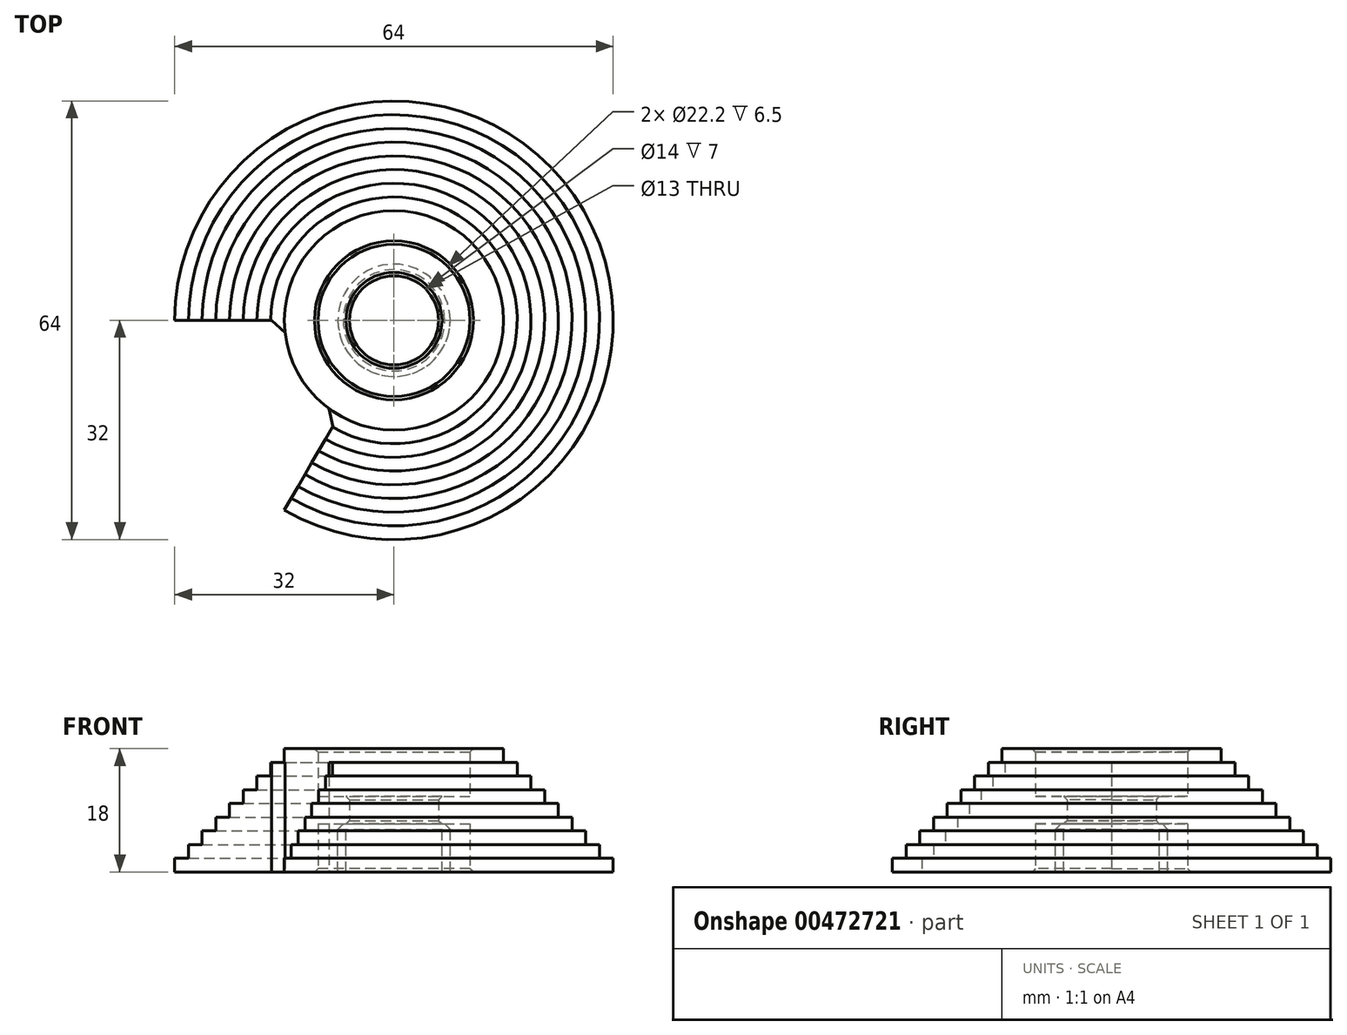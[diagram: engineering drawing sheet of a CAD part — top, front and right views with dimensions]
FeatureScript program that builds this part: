
annotation { "Feature Type Name" : "Feature", "Feature Type Description" : "" }
export const myFeature = defineFeature(function(context is Context, id is Id, definition is map)
    precondition{}
    {
        {
            var Q0;
            Q0=qCreatedBy(makeId("Front.planeOp"),FACE);
            var sketch = newSketch(context, id + "F0", { "sketchPlane" : qUnion([Q0])});
            skLineSegment(sketch, "E0", {"start": v(-11.1, 2) * mm, "end": v(-11.1, 9) * mm});
            skLineSegment(sketch, "E1", {"start": v(-11.1, 9) * mm, "end": v(-14, 9) * mm});
            skLineSegment(sketch, "E2", {"start": v(-14, 9) * mm, "end": v(-32, -9) * mm, "construction": true});
            skLineSegment(sketch, "E3", {"start": v(-32, -9) * mm, "end": v(-11.1, -9) * mm});
            skLineSegment(sketch, "E4", {"start": v(-11.1, -9) * mm, "end": v(-11.1, -2) * mm});
            skLineSegment(sketch, "E5", {"start": v(-11.1, 2) * mm, "end": v(-6.5, 2) * mm});
            skLineSegment(sketch, "E6", {"start": v(-6.5, 2) * mm, "end": v(-6.5, -2) * mm});
            skLineSegment(sketch, "E7", {"start": v(-6.5, -2) * mm, "end": v(-11.1, -2) * mm});
            skLineSegment(sketch, "E8", {"start": v(0, -9) * mm, "end": v(0, 9) * mm, "construction": true});
            skLineSegment(sketch, "E9", {"start": v(0, -9) * mm, "end": v(-32, -9) * mm, "construction": true});
            skLineSegment(sketch, "E10", {"start": v(-32, -9) * mm, "end": v(-32, -7) * mm});
            skLineSegment(sketch, "E11", {"start": v(-32, -7) * mm, "end": v(-30, -7) * mm});
            skLineSegment(sketch, "E12", {"start": v(-30, -7) * mm, "end": v(-30, -5) * mm});
            skLineSegment(sketch, "E13", {"start": v(-30, -5) * mm, "end": v(-28, -5) * mm});
            skLineSegment(sketch, "E14", {"start": v(-28, -5) * mm, "end": v(-28, -3) * mm});
            skLineSegment(sketch, "E15", {"start": v(-28, -3) * mm, "end": v(-26, -3) * mm});
            skLineSegment(sketch, "E16", {"start": v(-26, -3) * mm, "end": v(-26, -1) * mm});
            skLineSegment(sketch, "E17", {"start": v(-26, -1) * mm, "end": v(-24, -1) * mm});
            skLineSegment(sketch, "E18", {"start": v(-24, -1) * mm, "end": v(-24, 1) * mm});
            skLineSegment(sketch, "E19", {"start": v(-24, 1) * mm, "end": v(-22, 1) * mm});
            skLineSegment(sketch, "E20", {"start": v(-22, 1) * mm, "end": v(-22, 3) * mm});
            skLineSegment(sketch, "E21", {"start": v(-22, 3) * mm, "end": v(-20, 3) * mm});
            skLineSegment(sketch, "E22", {"start": v(-20, 3) * mm, "end": v(-20, 5) * mm});
            skLineSegment(sketch, "E23", {"start": v(-20, 5) * mm, "end": v(-18, 5) * mm});
            skLineSegment(sketch, "E24", {"start": v(-18, 5) * mm, "end": v(-18, 7) * mm});
            skLineSegment(sketch, "E25", {"start": v(-18, 7) * mm, "end": v(-16, 7) * mm});
            skLineSegment(sketch, "E26", {"start": v(-16, 7) * mm, "end": v(-16, 9) * mm});
            skLineSegment(sketch, "E27", {"start": v(-16, 9) * mm, "end": v(-14, 9) * mm});
            skSolve(sketch);
        }
        {
            var Q0;
            Q0 = qSketchRegion(id + "F0", true);
            var Q1;
            Q1=sQuery(id+"F0.wireOp",EDGE,"E8");
            revolve(context, id + "F1", {"entities" : qUnion([Q0]), "axis" : qUnion([Q1]), "revolveType" : RevolveType.FULL});
        }
        {
            var Q0;
            Q0=makeQuery(id+"F1.opRevolve","SWEPT_FACE",FACE,{"disambiguationData":[OSD([sQuery(id+"F0.wireOp",EDGE,"E3")])]});
            var sketch = newSketch(context, id + "F2", { "sketchPlane" : qUnion([Q0])});
            skLineSegment(sketch, "E28", {"start": v(0, 0) * mm, "end": v(-32, 0) * mm, "construction": true});
            skLineSegment(sketch, "E29", {"start": v(0, 0) * mm, "end": v(-16, 27.71) * mm, "construction": true});
            skLineSegment(sketch, "E30", {"start": v(-16, 0) * mm, "end": v(-32, 0) * mm});
            skLineSegment(sketch, "E31", {"start": v(-8, 13.86) * mm, "end": v(-16, 27.71) * mm});
            skCircle(sketch, "E32.0", {"center": v(0, 0) * mm, "radius": 11.1 * mm});
            skCircle(sketch, "E33.0", {"center": v(0, 0) * mm, "radius": 16 * mm});
            skSolve(sketch);
        }
        {
            var Q0;
            {var subQ0=sQuery(id+"F2.wireOp",EDGE,"E30");Q0=makeQuery(id+"F2.imprint","IMPRINT",FACE,{"disambiguationData":[TD([[makeQuery(id+"F2.imprint","IMPRINT",EDGE,{"derivedFrom":subQ0}),-1.0]])]});}
            extrude(context, id + "F3", {"entities" : qUnion([Q0]), "operationType" : NewBodyOperationType.REMOVE, "endBound" : BoundingType.THROUGH_ALL, "oppositeDirection" : true, "depth" : 25 * mm, "offsetDistance" : 25 * mm});
        }
        {
            var Q0;
            Q0=makeQuery(id+"F3.boolean.opBoolean","COPY",EDGE,{"derivedFrom":makeQuery(id+"F3.opExtrude","SWEPT_EDGE",EDGE,{"disambiguationData":[OSD([sQuery(id+"F2.wireOp",EDGE,"05b92925-b2af-4407-80f3-4efc4aef2622.0"),sQuery(id+"F2.wireOp",EDGE,"E30")])]})});
            var Q1;
            Q1=makeQuery(id+"F3.boolean.opBoolean","COPY",EDGE,{"derivedFrom":makeQuery(id+"F3.opExtrude","SWEPT_EDGE",EDGE,{"disambiguationData":[OSD([sQuery(id+"F2.wireOp",EDGE,"05b92925-b2af-4407-80f3-4efc4aef2622.0"),sQuery(id+"F2.wireOp",EDGE,"E31")])]})});
            var Q2;
            Q2=makeQuery(id+"FZNNoCGWcj2eKre_1.1.F3.boolean.opBoolean","COPY",EDGE,{"derivedFrom":makeQuery(id+"FZNNoCGWcj2eKre_1.1.F3.opExtrude","SWEPT_EDGE",EDGE,{"disambiguationData":[OSD([sQuery(id+"F2.wireOp",EDGE,"05b92925-b2af-4407-80f3-4efc4aef2622.0"),sQuery(id+"F2.wireOp",EDGE,"E31")])]})});
            var Q3;
            Q3=makeQuery(id+"FZNNoCGWcj2eKre_1.1.F3.boolean.opBoolean","COPY",EDGE,{"derivedFrom":makeQuery(id+"FZNNoCGWcj2eKre_1.1.F3.opExtrude","SWEPT_EDGE",EDGE,{"disambiguationData":[OSD([sQuery(id+"F2.wireOp",EDGE,"05b92925-b2af-4407-80f3-4efc4aef2622.0"),sQuery(id+"F2.wireOp",EDGE,"E30")])]})});
            var Q4;
            Q4=makeQuery(id+"FZNNoCGWcj2eKre_1.2.F3.boolean.opBoolean","COPY",EDGE,{"derivedFrom":makeQuery(id+"FZNNoCGWcj2eKre_1.2.F3.opExtrude","SWEPT_EDGE",EDGE,{"disambiguationData":[OSD([sQuery(id+"F2.wireOp",EDGE,"05b92925-b2af-4407-80f3-4efc4aef2622.0"),sQuery(id+"F2.wireOp",EDGE,"E31")])]})});
            var Q5;
            Q5=makeQuery(id+"FZNNoCGWcj2eKre_1.2.F3.boolean.opBoolean","COPY",EDGE,{"derivedFrom":makeQuery(id+"FZNNoCGWcj2eKre_1.2.F3.opExtrude","SWEPT_EDGE",EDGE,{"disambiguationData":[OSD([sQuery(id+"F2.wireOp",EDGE,"05b92925-b2af-4407-80f3-4efc4aef2622.0"),sQuery(id+"F2.wireOp",EDGE,"E30")])]})});
            chamfer(context, id + "F4", {"entities" : qUnion([Q0, Q1, Q2, Q3, Q4, Q5]), "width" : 2 * mm, "tangentPropagation" : true});
        }
        {
            var Q0;
            Q0=makeQuery(id+"F1.opRevolve","SWEPT_EDGE",EDGE,{"disambiguationData":[OSD([sQuery(id+"F0.wireOp",EDGE,"E3"),sQuery(id+"F0.wireOp",EDGE,"E4")])]});
            var Q1;
            Q1=makeQuery(id+"F1.opRevolve","SWEPT_EDGE",EDGE,{"disambiguationData":[OSD([sQuery(id+"F0.wireOp",EDGE,"E6"),sQuery(id+"F0.wireOp",EDGE,"E7")])]});
            var Q2;
            Q2=makeQuery(id+"F1.opRevolve","SWEPT_EDGE",EDGE,{"disambiguationData":[OSD([sQuery(id+"F0.wireOp",EDGE,"E5"),sQuery(id+"F0.wireOp",EDGE,"E6")])]});
            var Q3;
            Q3=makeQuery(id+"F1.opRevolve","SWEPT_EDGE",EDGE,{"disambiguationData":[OSD([sQuery(id+"F0.wireOp",EDGE,"E0"),sQuery(id+"F0.wireOp",EDGE,"E1")])]});
            chamfer(context, id + "F5", {"entities" : qUnion([Q0, Q1, Q2, Q3]), "width" : .5 * mm, "tangentPropagation" : true});
        }
        {
            var Q0;
            Q0=makeQuery(id+"F1.opRevolve","SWEPT_FACE",FACE,{"disambiguationData":[OSD([sQuery(id+"F0.wireOp",EDGE,"E7")])]});
            var sketch = newSketch(context, id + "F6", { "sketchPlane" : qUnion([Q0])});
            skCircle(sketch, "E34", {"center": v(0, 0) * mm, "radius": 8.2 * mm});
            skSolve(sketch);
        }
        {
            var Q0;
            Q0=makeQuery(id+"F6.imprint","IMPRINT",FACE,{"disambiguationData":[TD([[makeQuery(id+"F6.imprint","IMPRINT",EDGE,{"derivedFrom":sQuery(id+"F6.wireOp",EDGE,"E34")}),1.0]])]});
            var Q1;
            Q1=makeQuery(id+"F1.opRevolve","SWEPT_FACE",FACE,{"disambiguationData":[OSD([sQuery(id+"F0.wireOp",EDGE,"E3")])]});
            extrude(context, id + "F7", {"entities" : qUnion([Q0]), "endBound" : BoundingType.UP_TO_SURFACE, "depth" : 25 * mm, "endBoundEntityFace" : qUnion([Q1]), "offsetDistance" : 25 * mm});
        }
        {
            var Q0;
            Q0=makeQuery(id+"F7.opExtrude","CAP_EDGE",EDGE,{"disambiguationData":[OSD([sQuery(id+"F6.wireOp",EDGE,"E34")])],"isStart":true});
            chamfer(context, id + "F8", {"entities" : qUnion([Q0]), "width" : .8 * mm, "tangentPropagation" : true});
        }
    });
